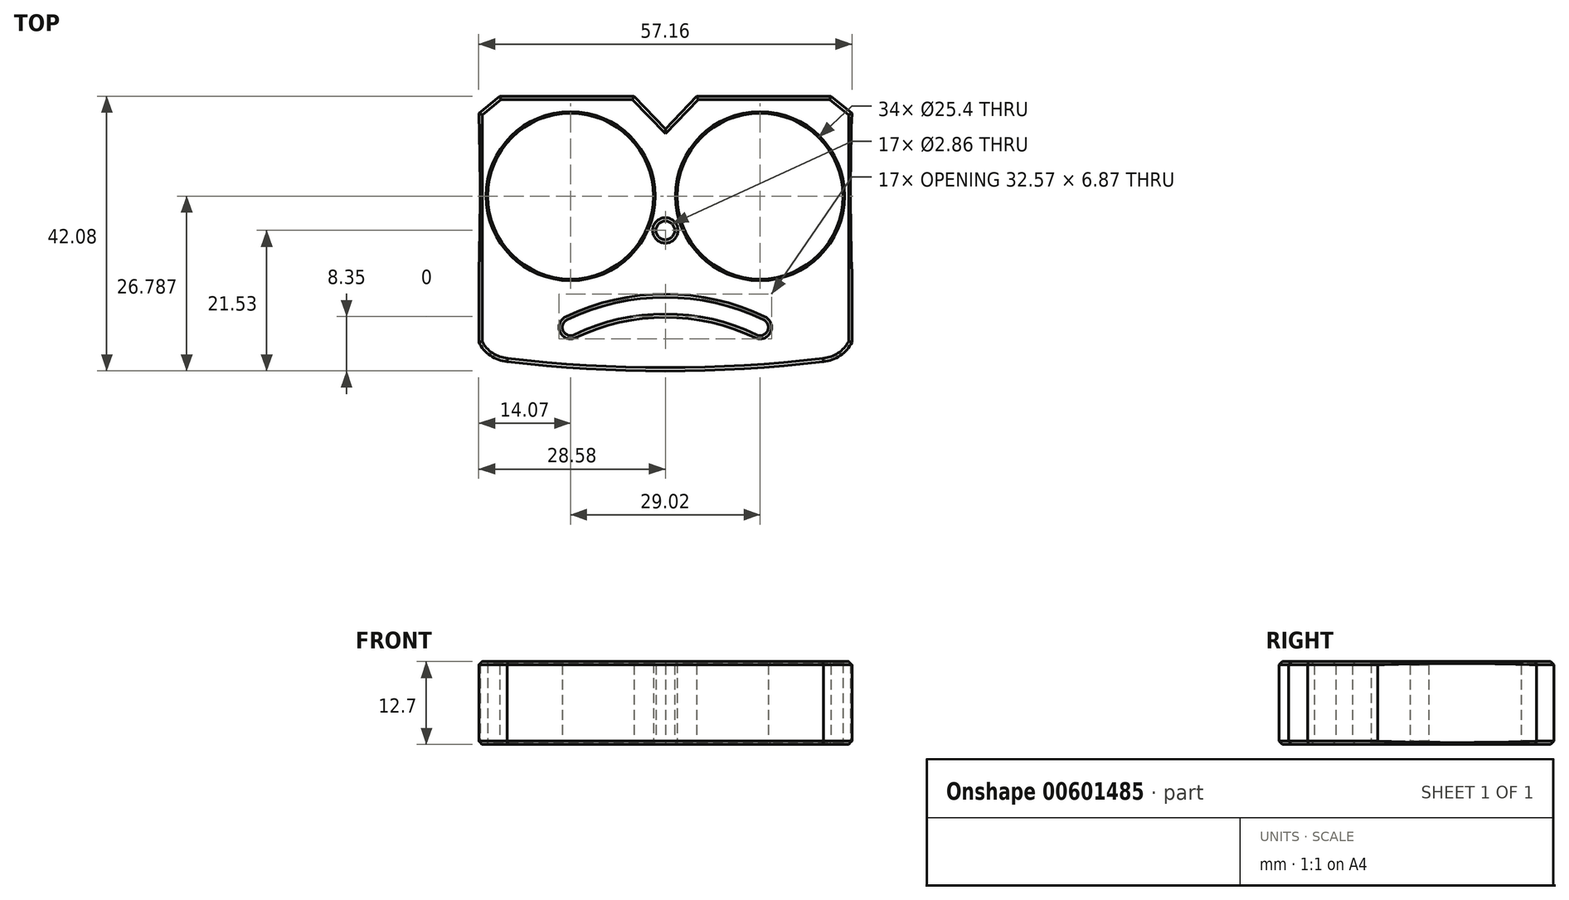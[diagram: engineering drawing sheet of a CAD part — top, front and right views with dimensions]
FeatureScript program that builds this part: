
annotation { "Feature Type Name" : "Feature", "Feature Type Description" : "" }
export const myFeature = defineFeature(function(context is Context, id is Id, definition is map)
    precondition{}
    {
        {
            var Q0;
            Q0=qCreatedBy(makeId("Top.planeOp"),FACE);
            var sketch = newSketch(context, id + "F0", { "sketchPlane" : qUnion([Q0])});
            skPoint(sketch, "E0.middle", {"position": v(0, 0) * mm});
            skCircle(sketch, "E1", {"center": v(-14.51, 5.26) * mm, "radius": 12.7 * mm});
            skCircle(sketch, "E2.MirrorC", {"center": v(14.51, 5.26) * mm, "radius": 12.7 * mm});
            skArc(sketch, "E3", {"start": v(-28.58, -17.11) * mm, "mid": v(-26.8, -19.18) * mm, "end": v(-24.21, -20.07) * mm});
            skArc(sketch, "E4.MirrorCS", {"start": v(28.58, -17.11) * mm, "mid": v(26.8, -19.18) * mm, "end": v(24.21, -20.07) * mm});
            skArc(sketch, "E5", {"start": v(-24.21, -20.07) * mm, "mid": v(0, -21.53) * mm, "end": v(24.21, -20.07) * mm});
            skLineSegment(sketch, "E6", {"start": v(-28.58, 17.92) * mm, "end": v(-25.36, 20.55) * mm});
            skLineSegment(sketch, "E7", {"start": v(-25.36, 20.55) * mm, "end": v(-4.8, 20.55) * mm});
            skLineSegment(sketch, "E8", {"start": v(-4.8, 20.55) * mm, "end": v(0, 15.54) * mm});
            skLineSegment(sketch, "E9.MirrorCS", {"start": v(4.8, 20.55) * mm, "end": v(0, 15.54) * mm});
            skLineSegment(sketch, "E10.MirrorCS", {"start": v(25.36, 20.55) * mm, "end": v(4.8, 20.55) * mm});
            skLineSegment(sketch, "E11.MirrorCS", {"start": v(28.58, 17.92) * mm, "end": v(25.36, 20.55) * mm});
            skArc(sketch, "E12", {"start": v(14.51, -14.84) * mm, "mid": v(0, -11.52) * mm, "end": v(-14.51, -14.84) * mm});
            skArc(sketch, "E13.0.startCap", {"start": v(15.06, -13.7) * mm, "mid": v(15.65, -15.4) * mm, "end": v(13.96, -15.98) * mm});
            skArc(sketch, "E13.0.endCap", {"start": v(-13.96, -15.98) * mm, "mid": v(-15.65, -15.4) * mm, "end": v(-15.06, -13.7) * mm});
            skArc(sketch, "E13.0.left", {"start": v(13.96, -15.98) * mm, "mid": v(0, -12.8) * mm, "end": v(-13.96, -15.98) * mm});
            skArc(sketch, "E13.0.right", {"start": v(15.06, -13.7) * mm, "mid": v(0, -10.25) * mm, "end": v(-15.06, -13.7) * mm});
            skCircle(sketch, "E14", {"center": v(0, 0) * mm, "radius": 1.43 * mm});
            skLineSegment(sketch, "E15", {"start": v(-28.58, -6.42) * mm, "end": v(-28.58, -17.11) * mm});
            skLineSegment(sketch, "E16", {"start": v(28.58, -6.42) * mm, "end": v(28.58, -17.11) * mm});
            skArc(sketch, "E17", {"start": v(-28.58, -6.42) * mm, "mid": v(-28.36, 5.75) * mm, "end": v(-28.58, 17.92) * mm});
            skArc(sketch, "E18.MirrorCS", {"start": v(28.58, -6.42) * mm, "mid": v(28.36, 5.75) * mm, "end": v(28.58, 17.92) * mm});
            skSolve(sketch);
        }
        {
            var Q0;
            Q0=makeQuery(id+"F0.imprint","IMPRINT",FACE,{"disambiguationData":[TD([[makeQuery(id+"F0.imprint","IMPRINT",EDGE,{"derivedFrom":sQuery(id+"F0.wireOp",EDGE,"E1")}),-1.0]])]});
            extrude(context, id + "F1", {"entities" : qUnion([Q0]), "depth" : 12.7 * mm, "offsetDistance" : 25.4 * mm});
        }
        {
            var Q0;
            Q0=makeQuery(id+"F1.opExtrude","CAP_EDGE",EDGE,{"disambiguationData":[OSD([sQuery(id+"F0.wireOp",EDGE,"E1")])],"isStart":false});
            var Q1;
            Q1=makeQuery(id+"F1.opExtrude","CAP_EDGE",EDGE,{"disambiguationData":[OSD([sQuery(id+"F0.wireOp",EDGE,"E1")])],"isStart":true});
            var Q2;
            Q2=makeQuery(id+"F1.opExtrude","CAP_EDGE",EDGE,{"disambiguationData":[OSD([sQuery(id+"F0.wireOp",EDGE,"E2.MirrorC")])],"isStart":true});
            var Q3;
            Q3=makeQuery(id+"F1.opExtrude","CAP_EDGE",EDGE,{"disambiguationData":[OSD([sQuery(id+"F0.wireOp",EDGE,"E2.MirrorC")])],"isStart":false});
            var Q4;
            Q4=makeQuery(id+"F1.opExtrude","CAP_EDGE",EDGE,{"disambiguationData":[OSD([sQuery(id+"F0.wireOp",EDGE,"luHKIT9h-mp6D-TrW3-YOZJ-P91xZvDW0tI3")])],"isStart":false});
            var Q5;
            Q5=makeQuery(id+"F1.opExtrude","CAP_EDGE",EDGE,{"disambiguationData":[OSD([sQuery(id+"F0.wireOp",EDGE,"luHKIT9h-mp6D-TrW3-YOZJ-P91xZvDW0tI3")])],"isStart":true});
            var Q6;
            Q6=makeQuery(id+"F1.opExtrude","CAP_EDGE",EDGE,{"disambiguationData":[OSD([sQuery(id+"F0.wireOp",EDGE,"9397db68-0aa8-4e88-b784-e13a772becce0.MirrorCS")])],"isStart":false});
            var Q7;
            Q7=makeQuery(id+"F1.opExtrude","CAP_EDGE",EDGE,{"disambiguationData":[OSD([sQuery(id+"F0.wireOp",EDGE,"9397db68-0aa8-4e88-b784-e13a772becce0.MirrorCS")])],"isStart":true});
            chamfer(context, id + "F2", {"entities" : qUnion([Q0, Q1, Q2, Q3, Q4, Q5, Q6, Q7]), "width" : 0.25 * mm, "tangentPropagation" : true});
        }
        {
            var Q0;
            Q0=makeQuery(id+"F1.opExtrude","CAP_EDGE",EDGE,{"disambiguationData":[OSD([sQuery(id+"F0.wireOp",EDGE,"E4.MirrorCS")])],"isStart":false});
            var Q1;
            Q1=makeQuery(id+"F1.opExtrude","CAP_EDGE",EDGE,{"disambiguationData":[OSD([sQuery(id+"F0.wireOp",EDGE,"E4.MirrorCS")])],"isStart":true});
            var Q2;
            Q2=makeQuery(id+"F1.opExtrude","CAP_EDGE",EDGE,{"disambiguationData":[OSD([sQuery(id+"F0.wireOp",EDGE,"E16")])],"isStart":true});
            var Q3;
            Q3=makeQuery(id+"F1.opExtrude","CAP_EDGE",EDGE,{"disambiguationData":[OSD([sQuery(id+"F0.wireOp",EDGE,"E16")])],"isStart":false});
            var Q4;
            Q4=makeQuery(id+"F1.opExtrude","CAP_EDGE",EDGE,{"disambiguationData":[OSD([sQuery(id+"F0.wireOp",EDGE,"E5")])],"isStart":true});
            var Q5;
            Q5=makeQuery(id+"F1.opExtrude","CAP_EDGE",EDGE,{"disambiguationData":[OSD([sQuery(id+"F0.wireOp",EDGE,"E5")])],"isStart":false});
            var Q6;
            Q6=makeQuery(id+"F1.opExtrude","CAP_EDGE",EDGE,{"disambiguationData":[OSD([sQuery(id+"F0.wireOp",EDGE,"E3")])],"isStart":false});
            var Q7;
            Q7=makeQuery(id+"F1.opExtrude","CAP_EDGE",EDGE,{"disambiguationData":[OSD([sQuery(id+"F0.wireOp",EDGE,"E3")])],"isStart":true});
            var Q8;
            Q8=makeQuery(id+"F1.opExtrude","CAP_EDGE",EDGE,{"disambiguationData":[OSD([sQuery(id+"F0.wireOp",EDGE,"E15")])],"isStart":false});
            var Q9;
            Q9=makeQuery(id+"F1.opExtrude","CAP_EDGE",EDGE,{"disambiguationData":[OSD([sQuery(id+"F0.wireOp",EDGE,"E15")])],"isStart":true});
            chamfer(context, id + "F3", {"entities" : qUnion([Q0, Q1, Q2, Q3, Q4, Q5, Q6, Q7, Q8, Q9]), "width" : 0.5 * mm, "tangentPropagation" : true});
        }
        {
            var Q0;
            Q0=makeQuery(id+"F1.opExtrude","CAP_EDGE",EDGE,{"disambiguationData":[OSD([sQuery(id+"F0.wireOp",EDGE,"E11.MirrorCS")])],"isStart":false});
            var Q1;
            Q1=makeQuery(id+"F1.opExtrude","CAP_EDGE",EDGE,{"disambiguationData":[OSD([sQuery(id+"F0.wireOp",EDGE,"E10.MirrorCS")])],"isStart":false});
            var Q2;
            Q2=makeQuery(id+"F1.opExtrude","CAP_EDGE",EDGE,{"disambiguationData":[OSD([sQuery(id+"F0.wireOp",EDGE,"E9.MirrorCS")])],"isStart":false});
            var Q3;
            Q3=makeQuery(id+"F1.opExtrude","CAP_EDGE",EDGE,{"disambiguationData":[OSD([sQuery(id+"F0.wireOp",EDGE,"E8")])],"isStart":false});
            var Q4;
            Q4=makeQuery(id+"F1.opExtrude","CAP_EDGE",EDGE,{"disambiguationData":[OSD([sQuery(id+"F0.wireOp",EDGE,"E7")])],"isStart":false});
            var Q5;
            Q5=makeQuery(id+"F1.opExtrude","CAP_EDGE",EDGE,{"disambiguationData":[OSD([sQuery(id+"F0.wireOp",EDGE,"E6")])],"isStart":false});
            var Q6;
            Q6=makeQuery(id+"F1.opExtrude","CAP_EDGE",EDGE,{"disambiguationData":[OSD([sQuery(id+"F0.wireOp",EDGE,"E6")])],"isStart":true});
            var Q7;
            Q7=makeQuery(id+"F1.opExtrude","CAP_EDGE",EDGE,{"disambiguationData":[OSD([sQuery(id+"F0.wireOp",EDGE,"E7")])],"isStart":true});
            var Q8;
            Q8=makeQuery(id+"F1.opExtrude","CAP_EDGE",EDGE,{"disambiguationData":[OSD([sQuery(id+"F0.wireOp",EDGE,"E9.MirrorCS")])],"isStart":true});
            var Q9;
            Q9=makeQuery(id+"F1.opExtrude","CAP_EDGE",EDGE,{"disambiguationData":[OSD([sQuery(id+"F0.wireOp",EDGE,"E8")])],"isStart":true});
            var Q10;
            Q10=makeQuery(id+"F1.opExtrude","CAP_EDGE",EDGE,{"disambiguationData":[OSD([sQuery(id+"F0.wireOp",EDGE,"E10.MirrorCS")])],"isStart":true});
            var Q11;
            Q11=makeQuery(id+"F1.opExtrude","CAP_EDGE",EDGE,{"disambiguationData":[OSD([sQuery(id+"F0.wireOp",EDGE,"E11.MirrorCS")])],"isStart":true});
            chamfer(context, id + "F4", {"entities" : qUnion([Q0, Q1, Q2, Q3, Q4, Q5, Q6, Q7, Q8, Q9, Q10, Q11]), "width" : 0.5 * mm, "tangentPropagation" : true});
        }
        {
            var Q0;
            Q0=makeQuery(id+"F1.opExtrude","CAP_EDGE",EDGE,{"disambiguationData":[OSD([sQuery(id+"F0.wireOp",EDGE,"E14")])],"isStart":false});
            var Q1;
            Q1=makeQuery(id+"F1.opExtrude","CAP_EDGE",EDGE,{"disambiguationData":[OSD([sQuery(id+"F0.wireOp",EDGE,"E14")])],"isStart":true});
            chamfer(context, id + "F5", {"entities" : qUnion([Q0, Q1]), "width" : 0.5 * mm, "tangentPropagation" : true});
        }
        {
            var Q0;
            Q0=makeQuery(id+"F1.opExtrude","CAP_EDGE",EDGE,{"disambiguationData":[OSD([sQuery(id+"F0.wireOp",EDGE,"E13.0.right")])],"isStart":false});
            var Q1;
            Q1=makeQuery(id+"F1.opExtrude","CAP_EDGE",EDGE,{"disambiguationData":[OSD([sQuery(id+"F0.wireOp",EDGE,"E13.0.left")])],"isStart":false});
            var Q2;
            Q2=makeQuery(id+"F1.opExtrude","CAP_EDGE",EDGE,{"disambiguationData":[OSD([sQuery(id+"F0.wireOp",EDGE,"E13.0.startCap")])],"isStart":false});
            var Q3;
            Q3=makeQuery(id+"F1.opExtrude","CAP_EDGE",EDGE,{"disambiguationData":[OSD([sQuery(id+"F0.wireOp",EDGE,"E13.0.endCap")])],"isStart":false});
            var Q4;
            Q4=makeQuery(id+"F1.opExtrude","CAP_EDGE",EDGE,{"disambiguationData":[OSD([sQuery(id+"F0.wireOp",EDGE,"E13.0.right")])],"isStart":true});
            var Q5;
            Q5=makeQuery(id+"F1.opExtrude","CAP_EDGE",EDGE,{"disambiguationData":[OSD([sQuery(id+"F0.wireOp",EDGE,"E13.0.startCap")])],"isStart":true});
            var Q6;
            Q6=makeQuery(id+"F1.opExtrude","CAP_EDGE",EDGE,{"disambiguationData":[OSD([sQuery(id+"F0.wireOp",EDGE,"E13.0.left")])],"isStart":true});
            var Q7;
            Q7=makeQuery(id+"F1.opExtrude","CAP_EDGE",EDGE,{"disambiguationData":[OSD([sQuery(id+"F0.wireOp",EDGE,"E13.0.endCap")])],"isStart":true});
            chamfer(context, id + "F6", {"entities" : qUnion([Q0, Q1, Q2, Q3, Q4, Q5, Q6, Q7]), "width" : 0.5 * mm, "tangentPropagation" : true});
        }
    });
